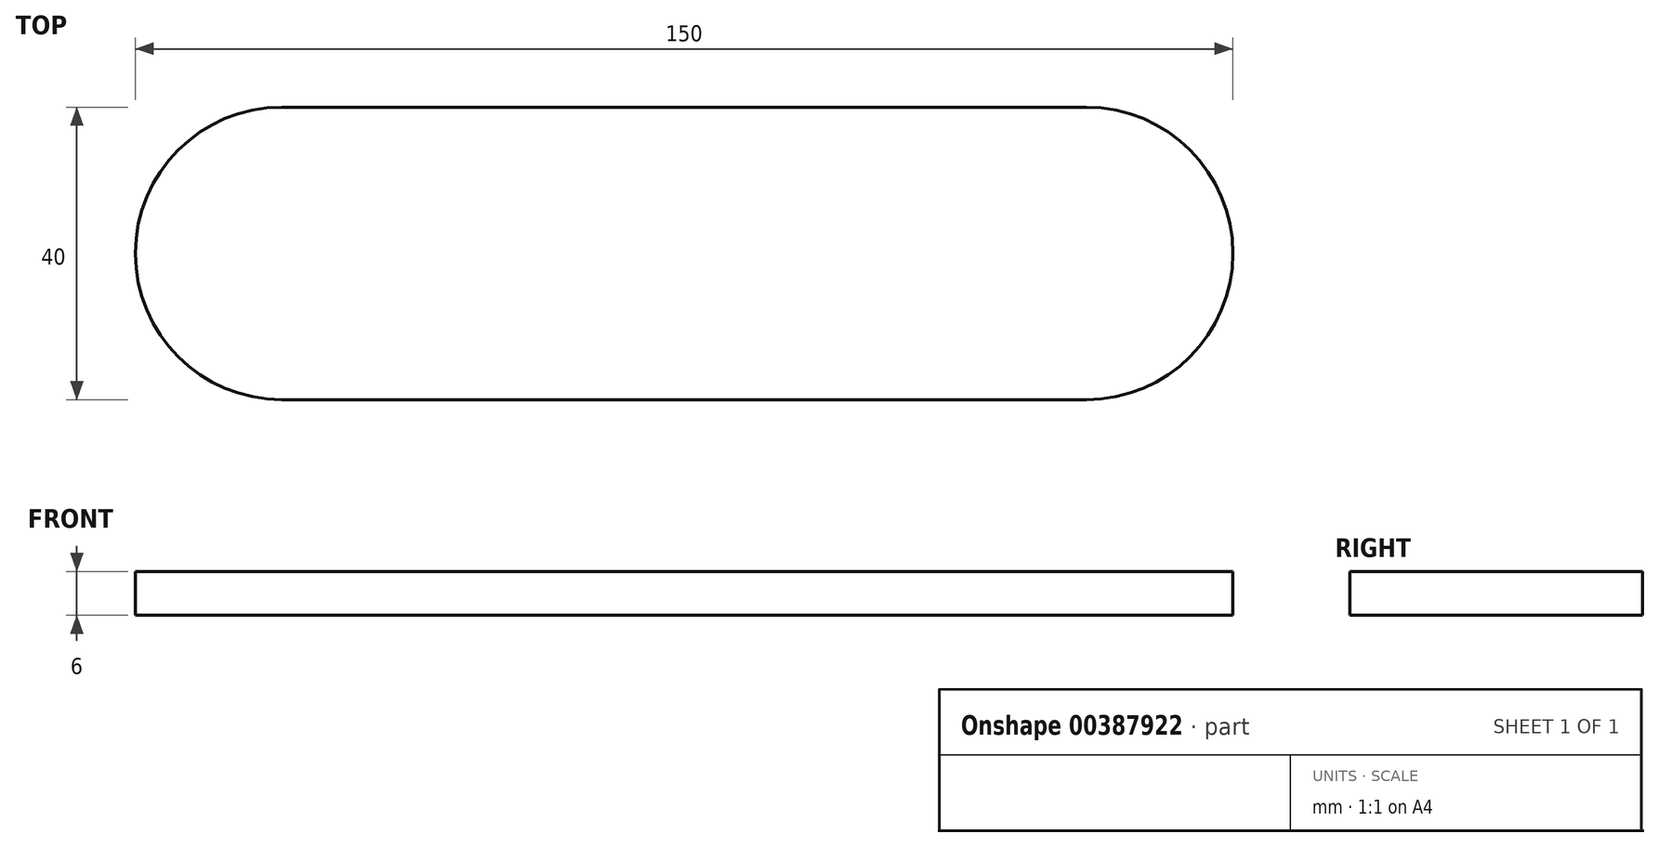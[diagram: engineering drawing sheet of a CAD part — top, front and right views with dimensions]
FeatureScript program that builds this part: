
annotation { "Feature Type Name" : "Feature", "Feature Type Description" : "" }
export const myFeature = defineFeature(function(context is Context, id is Id, definition is map)
    precondition{}
    {
        {
            var Q0;
            Q0=qCreatedBy(makeId("Top.planeOp"),FACE);
            var sketch = newSketch(context, id + "F0", { "sketchPlane" : qUnion([Q0])});
            skLineSegment(sketch, "E0.bottom", {"start": v(-53.28, 20.26) * mm, "end": v(56.72, 20.26) * mm});
            skLineSegment(sketch, "E0.top", {"start": v(-53.28, -19.74) * mm, "end": v(56.72, -19.74) * mm});
            skLineSegment(sketch, "E0.left", {"start": v(-53.28, 20.26) * mm, "end": v(-53.28, -19.74) * mm});
            skLineSegment(sketch, "E0.right", {"start": v(56.72, 20.26) * mm, "end": v(56.72, -19.74) * mm});
            skArc(sketch, "E1", {"start": v(-53.28, 20.26) * mm, "mid": v(-73.28, 0.26) * mm, "end": v(-53.28, -19.74) * mm});
            skArc(sketch, "E2", {"start": v(56.72, -19.74) * mm, "mid": v(76.72, 0.26) * mm, "end": v(56.72, 20.26) * mm});
            skSolve(sketch);
        }
        {
            var Q0;
            Q0=makeQuery(id+"F0.imprint","IMPRINT",FACE,{"disambiguationData":[TD([[makeQuery(id+"F0.imprint","IMPRINT",EDGE,{"derivedFrom":sQuery(id+"F0.wireOp",EDGE,"E0.left")}),-1.0]])]});
            var Q1;
            Q1=makeQuery(id+"F0.imprint","IMPRINT",FACE,{"disambiguationData":[TD([[makeQuery(id+"F0.imprint","IMPRINT",EDGE,{"derivedFrom":sQuery(id+"F0.wireOp",EDGE,"E0.right")}),1.0]])]});
            var Q2;
            Q2=makeQuery(id+"F0.imprint","IMPRINT",FACE,{"disambiguationData":[TD([[makeQuery(id+"F0.imprint","IMPRINT",EDGE,{"derivedFrom":sQuery(id+"F0.wireOp",EDGE,"E0.bottom")}),-1.0]])]});
            extrude(context, id + "F1", {"entities" : qUnion([Q0, Q1, Q2]), "depth" : 6 * mm});
        }
    });
